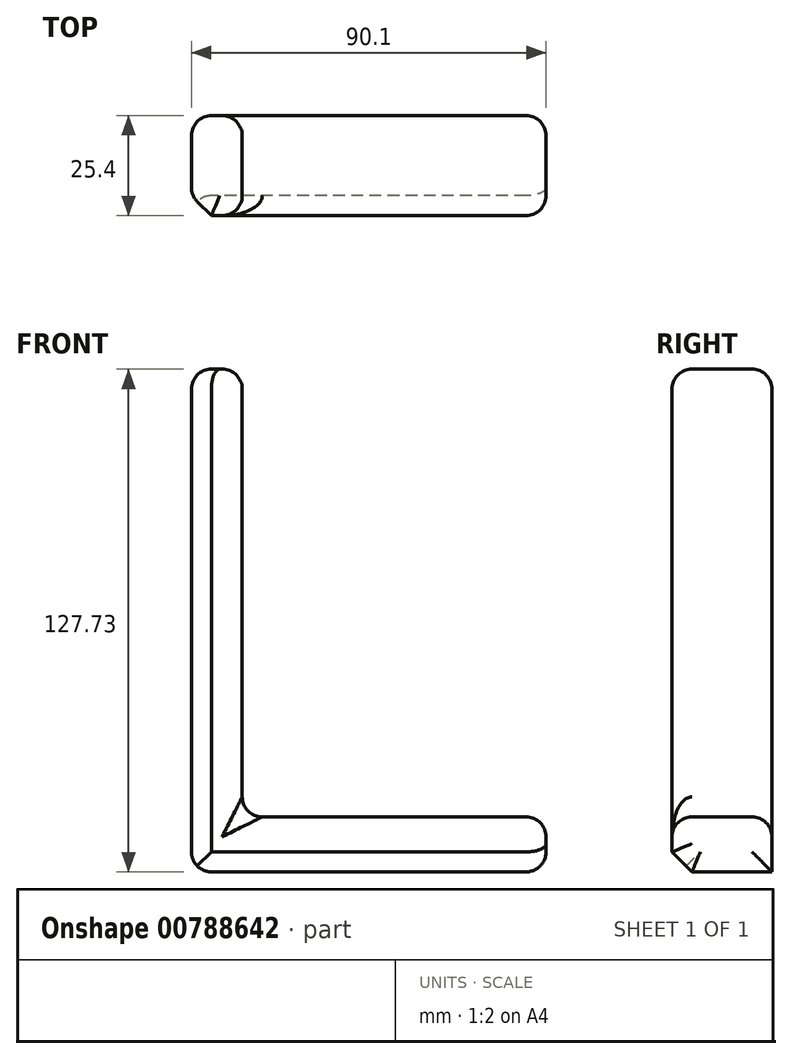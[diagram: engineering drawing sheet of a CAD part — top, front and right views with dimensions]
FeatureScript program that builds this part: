
annotation { "Feature Type Name" : "Feature", "Feature Type Description" : "" }
export const myFeature = defineFeature(function(context is Context, id is Id, definition is map)
    precondition{}
    {
        {
            var Q0;
            Q0=qCreatedBy(makeId("Front.planeOp"),FACE);
            var sketch = newSketch(context, id + "F0", { "sketchPlane" : qUnion([Q0])});
            skLineSegment(sketch, "E0.bottom", {"start": v(-45.78, 63.02) * mm, "end": v(-58.68, 63.02) * mm});
            skLineSegment(sketch, "E0.top", {"start": v(-45.78, -64.71) * mm, "end": v(-58.68, -64.71) * mm});
            skLineSegment(sketch, "E0.left", {"start": v(-45.78, 63.02) * mm, "end": v(-45.78, -64.71) * mm});
            skLineSegment(sketch, "E0.right", {"start": v(-58.68, 63.02) * mm, "end": v(-58.68, -64.71) * mm});
            skLineSegment(sketch, "E1.bottom", {"start": v(-45.78, -64.71) * mm, "end": v(31.42, -64.71) * mm});
            skLineSegment(sketch, "E1.top", {"start": v(-45.78, -50.72) * mm, "end": v(31.42, -50.72) * mm});
            skLineSegment(sketch, "E1.left", {"start": v(-45.78, -64.71) * mm, "end": v(-45.78, -50.72) * mm});
            skLineSegment(sketch, "E1.right", {"start": v(31.42, -64.71) * mm, "end": v(31.42, -50.72) * mm});
            skSolve(sketch);
        }
        {
            var Q0;
            Q0=makeQuery(id+"F0.imprint","IMPRINT",FACE,{"disambiguationData":[TD([[makeQuery(id+"F0.imprint","IMPRINT",EDGE,{"derivedFrom":sQuery(id+"F0.wireOp",EDGE,"E0.bottom")}),1.0]])]});
            var Q1;
            Q1=makeQuery(id+"F0.imprint","IMPRINT",FACE,{"disambiguationData":[TD([[makeQuery(id+"F0.imprint","IMPRINT",EDGE,{"derivedFrom":sQuery(id+"F0.wireOp",EDGE,"E1.bottom")}),1.0]])]});
            extrude(context, id + "F1", {"entities" : qUnion([Q0, Q1]), "depth" : 25.4 * mm, "offsetDistance" : 25.4 * mm});
        }
        {
            var Q0;
            Q0=makeQuery(id+"F1.opExtrude","CAP_EDGE",EDGE,{"disambiguationData":[OSD([sQuery(id+"F0.wireOp",EDGE,"E0.left")])],"isStart":false});
            var Q1;
            Q1=makeQuery(id+"F1.opExtrude","CAP_EDGE",EDGE,{"disambiguationData":[OSD([sQuery(id+"F0.wireOp",EDGE,"E1.top")])],"isStart":false});
            fillet(context, id + "F2", {"entities" : qUnion([Q0, Q1]), "radius" : 5.08 * mm, "tangentPropagation" : true, "allowEdgeOverflow" : false});
        }
        {
            var Q0;
            Q0=makeQuery(id+"F1.opExtrude","CAP_EDGE",EDGE,{"disambiguationData":[OSD([sQuery(id+"F0.wireOp",EDGE,"E0.right")])],"isStart":false});
            var Q1;
            Q1=makeQuery(id+"F1.opExtrude","CAP_EDGE",EDGE,{"disambiguationData":[OSD([sQuery(id+"F0.wireOp",EDGE,"E0.top"),sQuery(id+"F0.wireOp",EDGE,"E1.bottom")])],"isStart":false});
            chamfer(context, id + "F3", {"entities" : qUnion([Q0, Q1]), "width" : 5.08 * mm, "tangentPropagation" : true});
        }
        {
            var Q0;
            Q0=makeQuery(id+"F1.opExtrude","SWEPT_FACE",FACE,{"disambiguationData":[OSD([sQuery(id+"F0.wireOp",EDGE,"E0.right")])]});
            var Q1;
            Q1=makeQuery(id+"F1.opExtrude","SWEPT_FACE",FACE,{"disambiguationData":[OSD([sQuery(id+"F0.wireOp",EDGE,"E0.bottom")])]});
            var Q2;
            Q2=makeQuery(id+"F1.opExtrude","SWEPT_FACE",FACE,{"disambiguationData":[OSD([sQuery(id+"F0.wireOp",EDGE,"E0.left")])]});
            var Q3;
            Q3=makeQuery(id+"F1.opExtrude","SWEPT_FACE",FACE,{"disambiguationData":[OSD([sQuery(id+"F0.wireOp",EDGE,"E1.top")])]});
            var Q4;
            Q4=makeQuery(id+"F1.opExtrude","SWEPT_FACE",FACE,{"disambiguationData":[OSD([sQuery(id+"F0.wireOp",EDGE,"E1.right")])]});
            fillet(context, id + "F4", {"entities" : qUnion([Q0, Q1, Q2, Q3, Q4]), "radius" : 5.08 * mm, "tangentPropagation" : true, "allowEdgeOverflow" : false});
        }
    });
